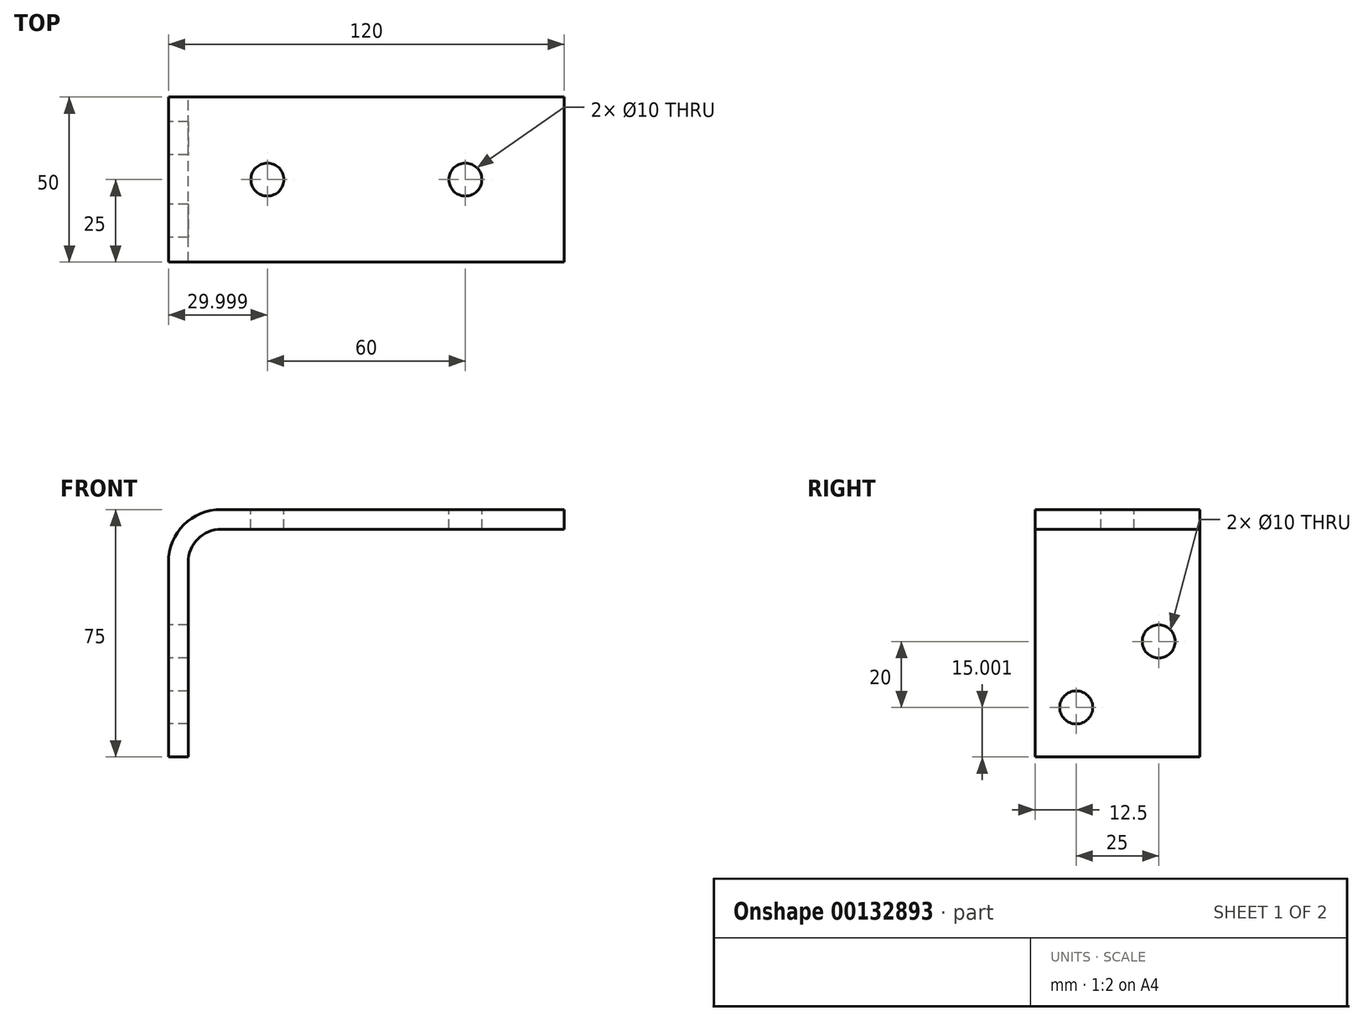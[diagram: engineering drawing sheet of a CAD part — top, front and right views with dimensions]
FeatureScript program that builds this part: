
annotation { "Feature Type Name" : "Feature", "Feature Type Description" : "" }
export const myFeature = defineFeature(function(context is Context, id is Id, definition is map)
    precondition{}
    {
        {
            var Q0;
            Q0=qCreatedBy(makeId("Front.planeOp"),FACE);
            var sketch = newSketch(context, id + "F0", { "sketchPlane" : qUnion([Q0])});
            skLineSegment(sketch, "E0", {"start": v(-53.07, -36.59) * mm, "end": v(-53.07, 22.41) * mm});
            skLineSegment(sketch, "E1", {"start": v(-37.07, 38.41) * mm, "end": v(66.93, 38.41) * mm});
            skLineSegment(sketch, "E2", {"start": v(66.93, 38.41) * mm, "end": v(66.93, 32.41) * mm});
            skLineSegment(sketch, "E3", {"start": v(-53.07, -36.59) * mm, "end": v(-47.07, -36.59) * mm});
            skPoint(sketch, "E4.visualSharp", {"position": v(-53.07, 38.41) * mm});
            skArc(sketch, "E4.filletArc", {"start": v(-37.07, 38.41) * mm, "mid": v(-48.38, 33.72) * mm, "end": v(-53.07, 22.41) * mm});
            skLineSegment(sketch, "E5", {"start": v(-47.07, -36.59) * mm, "end": v(-47.07, 22.41) * mm});
            skLineSegment(sketch, "E6", {"start": v(66.93, 32.41) * mm, "end": v(-37.07, 32.41) * mm});
            skPoint(sketch, "E7.newPointB", {"position": v(-47.07, 22.41) * mm});
            skArc(sketch, "E7.filletArc", {"start": v(-37.07, 32.41) * mm, "mid": v(-44.14, 29.48) * mm, "end": v(-47.07, 22.41) * mm});
            skSolve(sketch);
        }
        {
            var Q0;
            Q0=makeQuery(id+"F0.imprint","IMPRINT",FACE,{"disambiguationData":[TD([[makeQuery(id+"F0.imprint","IMPRINT",EDGE,{"derivedFrom":sQuery(id+"F0.wireOp",EDGE,"E0")}),-1.0]])]});
            extrude(context, id + "F1", {"entities" : qUnion([Q0]), "depth" : 50 * mm});
        }
        {
            var Q0;
            Q0=makeQuery(id+"F1.opExtrude","SWEPT_FACE",FACE,{"disambiguationData":[OSD([sQuery(id+"F0.wireOp",EDGE,"E1")])]});
            var sketch = newSketch(context, id + "F2", { "sketchPlane" : qUnion([Q0])});
            skLineSegment(sketch, "E8", {"start": v(66.93, -25) * mm, "end": v(-37.07, -25) * mm, "construction": true});
            skLineSegment(sketch, "E9", {"start": v(66.93, -25) * mm, "end": v(36.93, -25) * mm, "construction": true});
            skLineSegment(sketch, "E10", {"start": v(36.93, -25) * mm, "end": v(-23.07, -25) * mm, "construction": true});
            skCircle(sketch, "E11", {"center": v(-23.07, -25) * mm, "radius": 5 * mm});
            skCircle(sketch, "E12", {"center": v(36.93, -25) * mm, "radius": 5 * mm});
            skSolve(sketch);
        }
        {
            var Q0;
            Q0 = qSketchRegion(id + "F2", true);
            extrude(context, id + "F3", {"entities" : qUnion([Q0]), "operationType" : NewBodyOperationType.REMOVE, "oppositeDirection" : true, "depth" : 25 * mm});
        }
        {
            var Q0;
            Q0=makeQuery(id+"F1.opExtrude","SWEPT_FACE",FACE,{"disambiguationData":[OSD([sQuery(id+"F0.wireOp",EDGE,"E0")])]});
            var sketch = newSketch(context, id + "F4", { "sketchPlane" : qUnion([Q0])});
            skLineSegment(sketch, "E13", {"start": v(25, -36.59) * mm, "end": v(25, 39.24) * mm, "construction": true});
            skLineSegment(sketch, "E14", {"start": v(25, -36.59) * mm, "end": v(25, -21.28) * mm, "construction": true});
            skLineSegment(sketch, "E15", {"start": v(19.46, -36.59) * mm, "end": v(19.46, -21.59) * mm, "construction": true});
            skLineSegment(sketch, "E16", {"start": v(0, -15.57) * mm, "end": v(12.5, -15.57) * mm, "construction": true});
            skLineSegment(sketch, "E17", {"start": v(12.5, -15.57) * mm, "end": v(37.5, -15.57) * mm, "construction": true});
            skLineSegment(sketch, "E18", {"start": v(19.46, -21.59) * mm, "end": v(19.46, -1.59) * mm, "construction": true});
            skLineSegment(sketch, "E19", {"start": v(19.46, -1.59) * mm, "end": v(7.4, -1.59) * mm, "construction": true});
            skLineSegment(sketch, "E20", {"start": v(12.5, -15.57) * mm, "end": v(12.5, -5.17) * mm, "construction": true});
            skLineSegment(sketch, "E21", {"start": v(19.46, -21.59) * mm, "end": v(43.1, -21.59) * mm, "construction": true});
            skLineSegment(sketch, "E22", {"start": v(37.5, -15.57) * mm, "end": v(37.5, -26.25) * mm, "construction": true});
            skPoint(sketch, "E23", {"position": v(12.5, -1.59) * mm});
            skPoint(sketch, "E23.positionSnap0", {"position": v(13.43, -1.59) * mm});
            skPoint(sketch, "E24", {"position": v(37.5, -21.59) * mm});
            skCircle(sketch, "E25", {"center": v(12.5, -1.59) * mm, "radius": 5 * mm});
            skCircle(sketch, "E26", {"center": v(37.5, -21.59) * mm, "radius": 5 * mm});
            skSolve(sketch);
        }
        {
            var Q0;
            Q0 = qSketchRegion(id + "F4", true);
            extrude(context, id + "F5", {"entities" : qUnion([Q0]), "operationType" : NewBodyOperationType.REMOVE, "oppositeDirection" : true, "depth" : 25 * mm});
        }
    });
